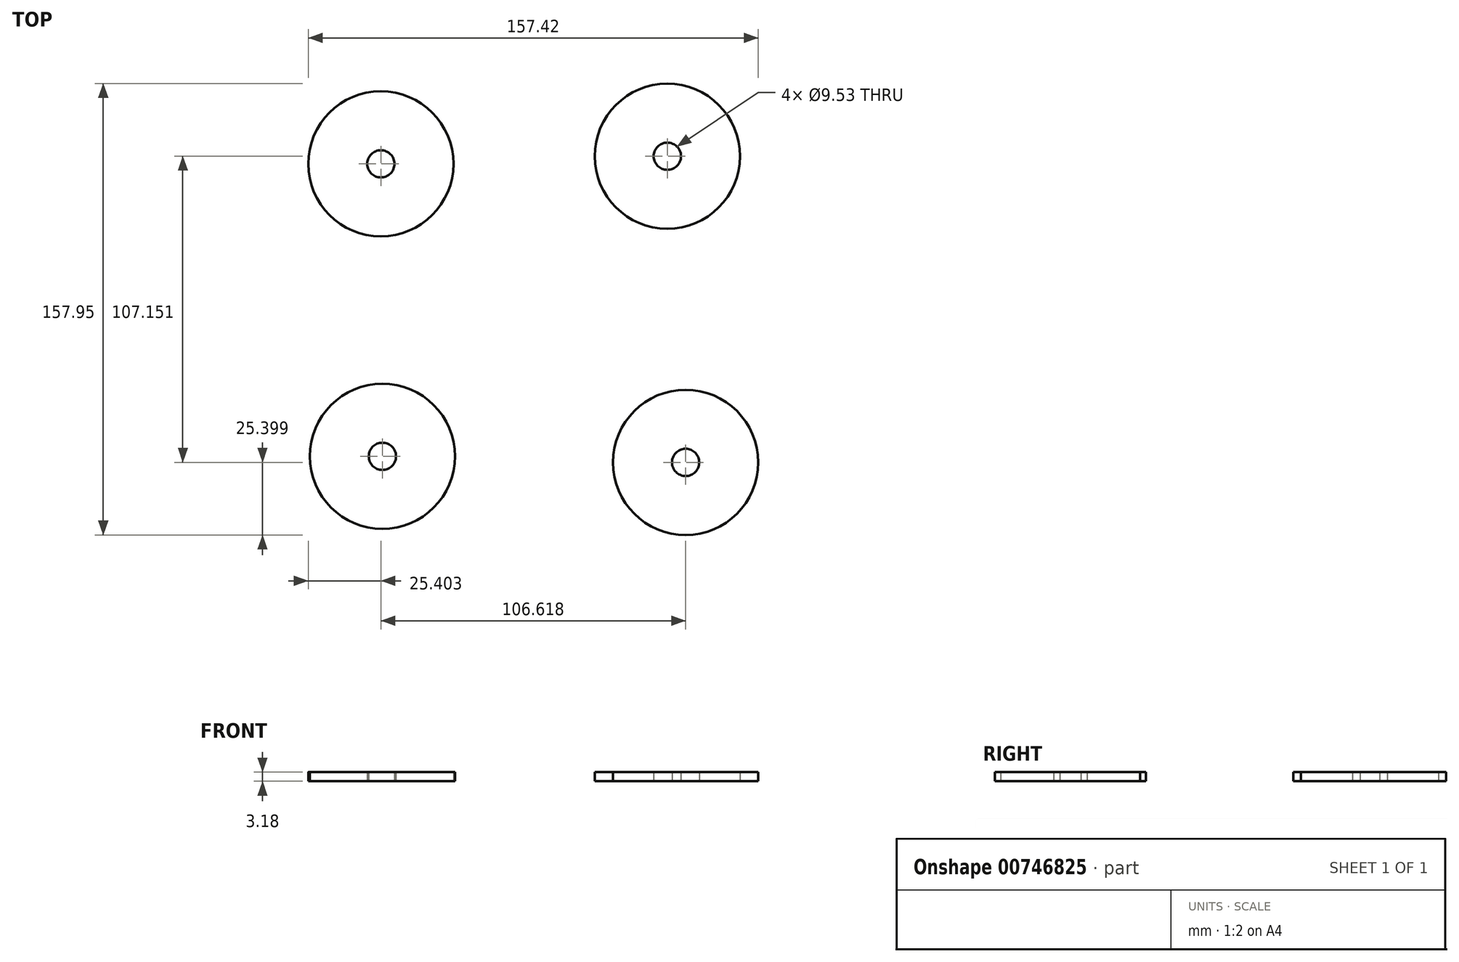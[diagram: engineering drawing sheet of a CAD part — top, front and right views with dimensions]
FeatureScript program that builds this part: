
annotation { "Feature Type Name" : "Feature", "Feature Type Description" : "" }
export const myFeature = defineFeature(function(context is Context, id is Id, definition is map)
    precondition{}
    {
        {
            var Q0;
            Q0=qCreatedBy(makeId("Top.planeOp"),FACE);
            var sketch = newSketch(context, id + "F0", { "sketchPlane" : qUnion([Q0])});
            skCircle(sketch, "E0", {"center": v(-55.07, 50.32) * mm, "radius": 25.4 * mm});
            skCircle(sketch, "E1", {"center": v(45.15, 52.99) * mm, "radius": 25.4 * mm});
            skCircle(sketch, "E2", {"center": v(51.55, -54.16) * mm, "radius": 25.4 * mm});
            skCircle(sketch, "E3", {"center": v(-54.53, -52.03) * mm, "radius": 25.4 * mm});
            skCircle(sketch, "E4", {"center": v(-55.07, 50.32) * mm, "radius": 4.76 * mm});
            skCircle(sketch, "E5", {"center": v(45.15, 52.99) * mm, "radius": 4.76 * mm});
            skCircle(sketch, "E6", {"center": v(51.55, -54.16) * mm, "radius": 4.76 * mm});
            skCircle(sketch, "E7", {"center": v(-54.53, -52.03) * mm, "radius": 4.76 * mm});
            skSolve(sketch);
        }
        {
            var Q0;
            Q0=makeQuery(id+"F0.imprint","IMPRINT",FACE,{"disambiguationData":[TD([[makeQuery(id+"F0.imprint","IMPRINT",EDGE,{"derivedFrom":sQuery(id+"F0.wireOp",EDGE,"E1")}),1.0]])]});
            var Q1;
            Q1=makeQuery(id+"F0.imprint","IMPRINT",FACE,{"disambiguationData":[TD([[makeQuery(id+"F0.imprint","IMPRINT",EDGE,{"derivedFrom":sQuery(id+"F0.wireOp",EDGE,"E2")}),1.0]])]});
            var Q2;
            Q2=makeQuery(id+"F0.imprint","IMPRINT",FACE,{"disambiguationData":[TD([[makeQuery(id+"F0.imprint","IMPRINT",EDGE,{"derivedFrom":sQuery(id+"F0.wireOp",EDGE,"E3")}),1.0]])]});
            var Q3;
            Q3=makeQuery(id+"F0.imprint","IMPRINT",FACE,{"disambiguationData":[TD([[makeQuery(id+"F0.imprint","IMPRINT",EDGE,{"derivedFrom":sQuery(id+"F0.wireOp",EDGE,"E0")}),1.0]])]});
            extrude(context, id + "F1", {"entities" : qUnion([Q0, Q1, Q2, Q3]), "depth" : 3.17 * mm, "offsetDistance" : 25.4 * mm});
        }
    });
